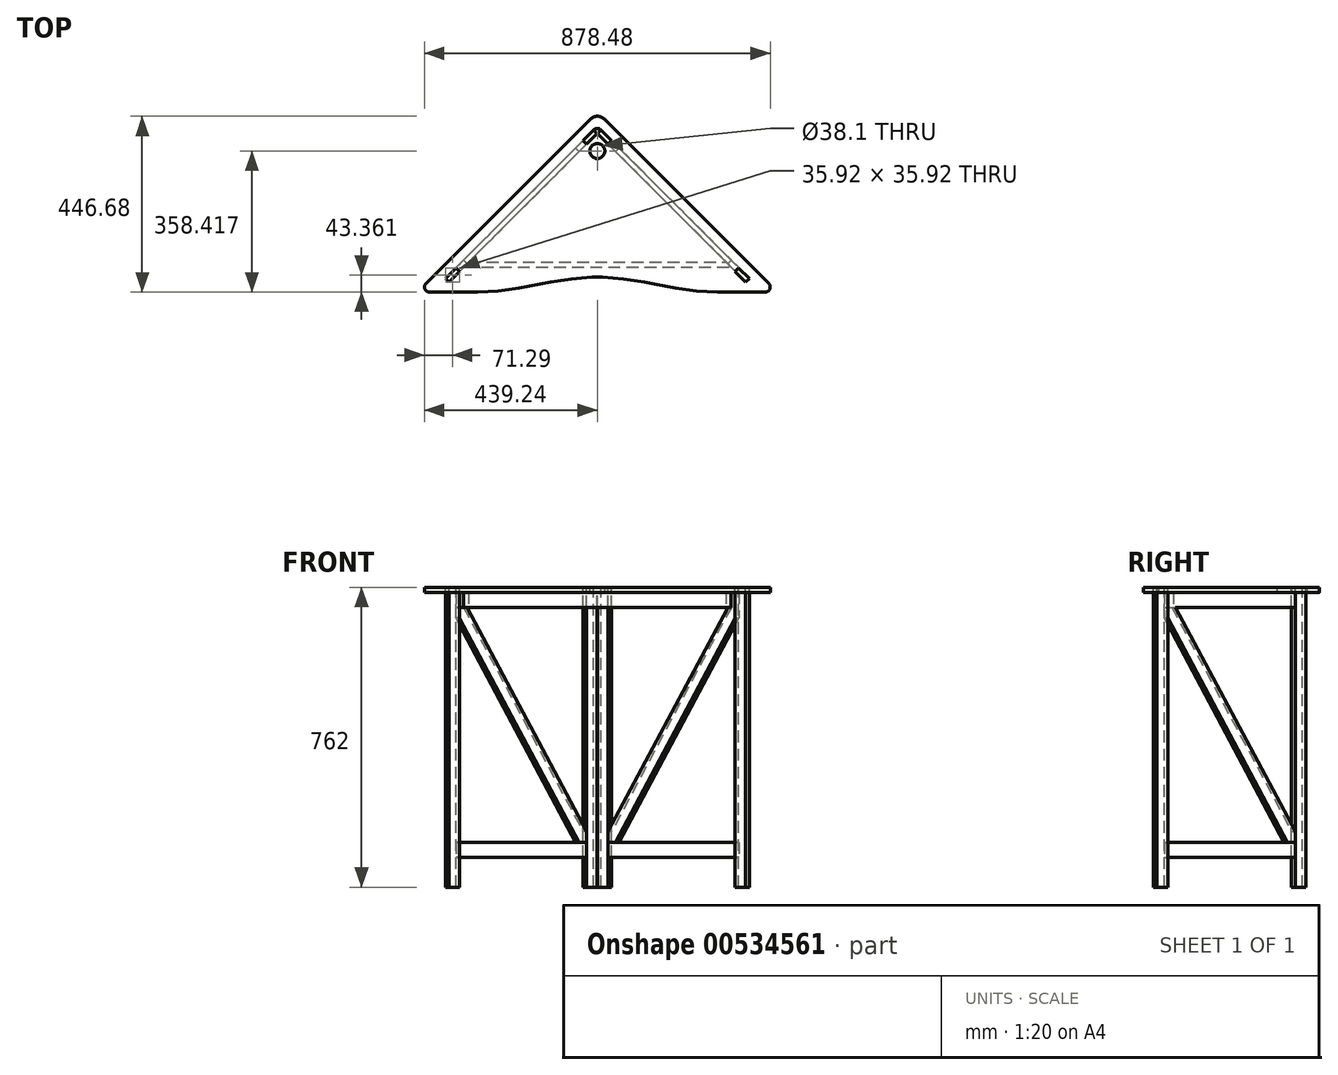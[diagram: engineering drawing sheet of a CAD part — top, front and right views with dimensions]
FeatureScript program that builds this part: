
annotation { "Feature Type Name" : "Feature", "Feature Type Description" : "" }
export const myFeature = defineFeature(function(context is Context, id is Id, definition is map)
    precondition{}
    {
        {
            var Q0;
            Q0=qCreatedBy(makeId("Top.planeOp"),FACE);
            var sketch = newSketch(context, id + "F0", { "sketchPlane" : qUnion([Q0])});
            skLineSegment(sketch, "E0", {"start": v(0, 457.2) * mm, "end": v(228.6, 228.6) * mm, "construction": true});
            skLineSegment(sketch, "E1", {"start": v(457.2, 0) * mm, "end": v(0, 0) * mm, "construction": true});
            skLineSegment(sketch, "E2", {"start": v(-228.6, 228.6) * mm, "end": v(0, 0) * mm, "construction": true});
            skLineSegment(sketch, "E3", {"start": v(0, 0) * mm, "end": v(228.6, 228.6) * mm, "construction": true});
            skLineSegment(sketch, "E4", {"start": v(0, 0) * mm, "end": v(0, 457.2) * mm, "construction": true});
            skLineSegment(sketch, "E5", {"start": v(-228.6, 228.6) * mm, "end": v(0, 457.2) * mm, "construction": true});
            skLineSegment(sketch, "E6", {"start": v(228.6, 228.6) * mm, "end": v(457.2, 0) * mm, "construction": true});
            skLineSegment(sketch, "E7", {"start": v(0, 0) * mm, "end": v(-457.2, 0) * mm, "construction": true});
            skPoint(sketch, "E8.visualSharp", {"position": v(-457.2, 0) * mm});
            skPoint(sketch, "E9.visualSharp", {"position": v(457.2, 0) * mm});
            skPoint(sketch, "E10.visualSharp", {"position": v(0, 457.2) * mm});
            skLineSegment(sketch, "E11", {"start": v(-228.6, 228.6) * mm, "end": v(-457.2, 0) * mm, "construction": true});
            skSolve(sketch);
        }
        {
            var Q0;
            Q0=qCreatedBy(makeId("Top.planeOp"),FACE);
            var sketch = newSketch(context, id + "F1", { "sketchPlane" : qUnion([Q0])});
            skLineSegment(sketch, "E12", {"start": v(17.96, 439.24) * mm, "end": v(435.52, 21.68) * mm});
            skLineSegment(sketch, "E13", {"start": v(-435.52, 21.68) * mm, "end": v(-17.96, 439.24) * mm});
            skLineSegment(sketch, "E14", {"start": v(-426.54, 0) * mm, "end": v(-304.8, 0) * mm});
            skLineSegment(sketch, "E15", {"start": v(304.8, 0) * mm, "end": v(426.54, 0) * mm});
            skLineSegment(sketch, "E16", {"start": v(-304.8, 0) * mm, "end": v(-203.2, 0) * mm, "construction": true});
            skLineSegment(sketch, "E17", {"start": v(304.8, 0) * mm, "end": v(203.2, 0) * mm, "construction": true});
            skFitSpline(sketch, "E18", {"points": [v(-304.8, 0) * mm, v(0, 38.1) * mm, v(304.8, 0) * mm], "startDerivative": vector(609.6, 0) * mm, "endDerivative": vector(609.6, 0) * mm});
            skPoint(sketch, "E19.visualSharp", {"position": v(-457.2, 0) * mm});
            skArc(sketch, "E19.filletArc", {"start": v(-435.52, 21.68) * mm, "mid": v(-438.27, 7.84) * mm, "end": v(-426.54, 0) * mm});
            skPoint(sketch, "E20.visualSharp", {"position": v(457.2, 0) * mm});
            skArc(sketch, "E20.filletArc", {"start": v(426.54, 0) * mm, "mid": v(438.27, 7.84) * mm, "end": v(435.52, 21.68) * mm});
            skPoint(sketch, "E21.visualSharp", {"position": v(0, 457.2) * mm});
            skArc(sketch, "E21.filletArc", {"start": v(17.96, 439.24) * mm, "mid": v(0, 446.68) * mm, "end": v(-17.96, 439.24) * mm});
            skSolve(sketch);
        }
        {
            var Q0;
            Q0=qCreatedBy(makeId("Top.planeOp"),FACE);
            var sketch = newSketch(context, id + "F2", { "sketchPlane" : qUnion([Q0])});
            skLineSegment(sketch, "E22", {"start": v(-0.25, 403.06) * mm, "end": v(-27.2, 376.12) * mm});
            skLineSegment(sketch, "E23", {"start": v(-27.2, 376.12) * mm, "end": v(-36.18, 385.1) * mm});
            skLineSegment(sketch, "E24", {"start": v(-36.18, 385.1) * mm, "end": v(-9.23, 412.04) * mm});
            skLineSegment(sketch, "E25", {"start": v(-9.23, 412.04) * mm, "end": v(-0.25, 403.06) * mm});
            skLineSegment(sketch, "E26.MirrorCS", {"start": v(-385.91, 34.38) * mm, "end": v(-376.93, 25.4) * mm});
            skLineSegment(sketch, "E27.MirrorCS", {"start": v(-349.99, 52.34) * mm, "end": v(-358.97, 61.32) * mm});
            skLineSegment(sketch, "E28.MirrorCS", {"start": v(-358.97, 61.32) * mm, "end": v(-385.91, 34.38) * mm});
            skLineSegment(sketch, "E29.MirrorCS", {"start": v(-376.93, 25.4) * mm, "end": v(-349.99, 52.34) * mm});
            skLineSegment(sketch, "E30.MirrorCS", {"start": v(349.99, 52.34) * mm, "end": v(358.97, 61.32) * mm});
            skLineSegment(sketch, "E31.MirrorCS", {"start": v(385.91, 34.38) * mm, "end": v(376.93, 25.4) * mm});
            skLineSegment(sketch, "E32.MirrorCS", {"start": v(376.93, 25.4) * mm, "end": v(349.99, 52.34) * mm});
            skLineSegment(sketch, "E33.MirrorCS", {"start": v(358.97, 61.32) * mm, "end": v(385.91, 34.38) * mm});
            skLineSegment(sketch, "E34.MirrorCS", {"start": v(9.23, 412.04) * mm, "end": v(0.25, 403.06) * mm});
            skLineSegment(sketch, "E35.MirrorCS", {"start": v(27.2, 376.12) * mm, "end": v(36.18, 385.1) * mm});
            skLineSegment(sketch, "E36.MirrorCS", {"start": v(36.18, 385.1) * mm, "end": v(9.23, 412.04) * mm});
            skLineSegment(sketch, "E37.MirrorCS", {"start": v(0.25, 403.06) * mm, "end": v(27.2, 376.12) * mm});
            skCircle(sketch, "E38", {"center": v(0, 358.42) * mm, "radius": 19.05 * mm});
            skArc(sketch, "E39", {"start": v(9.23, 412.04) * mm, "mid": v(0, 415.87) * mm, "end": v(-9.23, 412.04) * mm});
            skArc(sketch, "E40", {"start": v(0.25, 403.06) * mm, "mid": v(0, 403.17) * mm, "end": v(-0.25, 403.06) * mm});
            skSolve(sketch);
        }
        {
            var Q0;
            Q0=makeQuery(id+"F1.imprint","IMPRINT",FACE,{"disambiguationData":[TD([[makeQuery(id+"F1.imprint","IMPRINT",EDGE,{"derivedFrom":sQuery(id+"F1.wireOp",EDGE,"E12")}),-1.0]])]});
            extrude(context, id + "F3", {"entities" : qUnion([Q0]), "oppositeDirection" : true, "depth" : 12.7 * mm, "offsetDistance" : 25.4 * mm});
        }
        {
            var Q0;
            Q0 = qSketchRegion(id + "F2", true);
            extrude(context, id + "F4", {"entities" : qUnion([Q0]), "operationType" : NewBodyOperationType.REMOVE, "endBound" : BoundingType.UP_TO_NEXT, "oppositeDirection" : true, "depth" : 25.4 * mm, "offsetDistance" : 25.4 * mm});
        }
        {
            var Q0;
            Q0=makeQuery(id+"F2.imprint","IMPRINT",FACE,{"disambiguationData":[TD([[makeQuery(id+"F2.imprint","IMPRINT",EDGE,{"derivedFrom":sQuery(id+"F2.wireOp",EDGE,"E26.MirrorCS")}),1.0]])]});
            var Q1;
            Q1=makeQuery(id+"F2.imprint","IMPRINT",FACE,{"disambiguationData":[TD([[makeQuery(id+"F2.imprint","IMPRINT",EDGE,{"derivedFrom":sQuery(id+"F2.wireOp",EDGE,"E30.MirrorCS")}),-1.0]])]});
            var Q2;
            Q2=makeQuery(id+"F2.imprint","IMPRINT",FACE,{"disambiguationData":[TD([[makeQuery(id+"F2.imprint","IMPRINT",EDGE,{"derivedFrom":sQuery(id+"F2.wireOp",EDGE,"E34.MirrorCS")}),1.0]])]});
            var Q3;
            Q3=makeQuery(id+"F2.imprint","IMPRINT",FACE,{"disambiguationData":[TD([[makeQuery(id+"F2.imprint","IMPRINT",EDGE,{"derivedFrom":sQuery(id+"F2.wireOp",EDGE,"E22")}),-1.0]])]});
            var Q4;
            Q4=sQuery(id+"F2.wireOp",EDGE,"E22");
            var Q5;
            Q5=sQuery(id+"F2.wireOp",EDGE,"E23");
            var Q6;
            Q6=sQuery(id+"F2.wireOp",EDGE,"E24");
            var Q7;
            Q7=sQuery(id+"F2.wireOp",EDGE,"E25");
            var Q8;
            Q8=sQuery(id+"F2.wireOp",EDGE,"E26.MirrorCS");
            var Q9;
            Q9=sQuery(id+"F2.wireOp",EDGE,"E27.MirrorCS");
            var Q10;
            Q10=sQuery(id+"F2.wireOp",EDGE,"E28.MirrorCS");
            var Q11;
            Q11=sQuery(id+"F2.wireOp",EDGE,"E29.MirrorCS");
            var Q12;
            Q12=sQuery(id+"F2.wireOp",EDGE,"E30.MirrorCS");
            var Q13;
            Q13=sQuery(id+"F2.wireOp",EDGE,"E31.MirrorCS");
            var Q14;
            Q14=sQuery(id+"F2.wireOp",EDGE,"E32.MirrorCS");
            var Q15;
            Q15=sQuery(id+"F2.wireOp",EDGE,"E33.MirrorCS");
            var Q16;
            Q16=sQuery(id+"F2.wireOp",EDGE,"E34.MirrorCS");
            var Q17;
            Q17=sQuery(id+"F2.wireOp",EDGE,"E35.MirrorCS");
            var Q18;
            Q18=sQuery(id+"F2.wireOp",EDGE,"E36.MirrorCS");
            var Q19;
            Q19=sQuery(id+"F2.wireOp",EDGE,"E37.MirrorCS");
            var Q20;
            Q20=sQuery(id+"F2.wireOp",EDGE,"E40");
            extrude(context, id + "F5", {"entities" : qUnion([Q0, Q1, Q2, Q3]), "surfaceEntities" : qUnion([Q4, Q5, Q6, Q7, Q8, Q9, Q10, Q11, Q12, Q13, Q14, Q15, Q16, Q17, Q18, Q19, Q20]), "oppositeDirection" : true, "depth" : 762 * mm, "offsetDistance" : 25.4 * mm});
        }
        {
            var Q0;
            Q0=makeQuery(id+"F5.opExtrude","SWEPT_FACE",FACE,{"disambiguationData":[OSD([sQuery(id+"F2.wireOp",EDGE,"E23")])]});
            var sketch = newSketch(context, id + "F6", { "sketchPlane" : qUnion([Q0])});
            skLineSegment(sketch, "E41.bottom", {"start": v(-297.89, -12.7) * mm, "end": v(-285.19, -12.7) * mm});
            skLineSegment(sketch, "E41.top", {"start": v(-297.89, -50.8) * mm, "end": v(-285.19, -50.8) * mm});
            skLineSegment(sketch, "E41.left", {"start": v(-297.89, -12.7) * mm, "end": v(-297.89, -50.8) * mm});
            skLineSegment(sketch, "E41.right", {"start": v(-285.19, -12.7) * mm, "end": v(-285.19, -50.8) * mm});
            skLineSegment(sketch, "E42.bottom", {"start": v(-297.89, -647.7) * mm, "end": v(-285.19, -647.7) * mm});
            skLineSegment(sketch, "E42.top", {"start": v(-297.89, -685.8) * mm, "end": v(-285.19, -685.8) * mm});
            skLineSegment(sketch, "E42.left", {"start": v(-297.89, -647.7) * mm, "end": v(-297.89, -685.8) * mm});
            skLineSegment(sketch, "E42.right", {"start": v(-285.19, -647.7) * mm, "end": v(-285.19, -685.8) * mm});
            skSolve(sketch);
        }
        {
            var Q0;
            Q0 = qSketchRegion(id + "F6", true);
            var Q1;
            Q1=makeQuery(id+"F5.opExtrude","SWEPT_FACE",FACE,{"disambiguationData":[OSD([sQuery(id+"F2.wireOp",EDGE,"E27.MirrorCS")])]});
            var Q2;
            Q2=makeQuery(id+"F5.opExtrude","SWEPT_BODY",BODY,{"disambiguationData":[OSD([sQuery(id+"F2.wireOp",EDGE,"E26.MirrorCS"),sQuery(id+"F2.wireOp",EDGE,"E27.MirrorCS"),sQuery(id+"F2.wireOp",EDGE,"E28.MirrorCS"),sQuery(id+"F2.wireOp",EDGE,"E29.MirrorCS")])]});
            extrude(context, id + "F7", {"entities" : qUnion([Q0]), "endBound" : BoundingType.UP_TO_SURFACE, "depth" : 762 * mm, "endBoundEntityFace" : qUnion([Q1]), "endBoundEntityBody" : qUnion([Q2]), "offsetDistance" : 25.4 * mm});
        }
        {
            var Q0;
            Q0=makeQuery(id+"F5.opExtrude","SWEPT_FACE",FACE,{"disambiguationData":[OSD([sQuery(id+"F2.wireOp",EDGE,"E24")])]});
            var sketch = newSketch(context, id + "F8", { "sketchPlane" : qUnion([Q0])});
            skLineSegment(sketch, "E43", {"start": v(210.47, -50.8) * mm, "end": v(183.27, -50.8) * mm});
            skLineSegment(sketch, "E44", {"start": v(183.27, -50.8) * mm, "end": v(-246.73, -620.5) * mm});
            skLineSegment(sketch, "E45", {"start": v(-246.73, -620.5) * mm, "end": v(-246.73, -647.7) * mm});
            skLineSegment(sketch, "E46", {"start": v(-246.73, -647.7) * mm, "end": v(-219.53, -647.7) * mm});
            skLineSegment(sketch, "E47", {"start": v(-219.53, -647.7) * mm, "end": v(210.47, -78) * mm});
            skLineSegment(sketch, "E48", {"start": v(210.47, -78) * mm, "end": v(210.47, -50.8) * mm});
            skSolve(sketch);
        }
        {
            var Q0;
            Q0=makeQuery(id+"F8.imprint","IMPRINT",FACE,{"disambiguationData":[TD([[makeQuery(id+"F8.imprint","IMPRINT",EDGE,{"derivedFrom":sQuery(id+"F8.wireOp",EDGE,"E43")}),1.0]])]});
            extrude(context, id + "F9", {"entities" : qUnion([Q0]), "oppositeDirection" : true, "depth" : 12.7 * mm, "offsetDistance" : 25.4 * mm});
        }
        {
            var Q0;
            Q0=makeQuery(id+"F7.opExtrude","SWEPT_BODY",BODY,{"disambiguationData":[OSD([sQuery(id+"F6.wireOp",EDGE,"E42.bottom"),sQuery(id+"F6.wireOp",EDGE,"E42.top"),sQuery(id+"F6.wireOp",EDGE,"E42.left"),sQuery(id+"F6.wireOp",EDGE,"E42.right")])]});
            var Q1;
            Q1=makeQuery(id+"F7.opExtrude","SWEPT_BODY",BODY,{"disambiguationData":[OSD([sQuery(id+"F6.wireOp",EDGE,"E41.bottom"),sQuery(id+"F6.wireOp",EDGE,"E41.top"),sQuery(id+"F6.wireOp",EDGE,"E41.left"),sQuery(id+"F6.wireOp",EDGE,"E41.right")])]});
            var Q2;
            Q2=makeQuery(id+"F9.opExtrude","SWEPT_BODY",BODY,{"disambiguationData":[OSD([sQuery(id+"F8.wireOp",EDGE,"E43"),sQuery(id+"F8.wireOp",EDGE,"E44"),sQuery(id+"F8.wireOp",EDGE,"E45"),sQuery(id+"F8.wireOp",EDGE,"E46"),sQuery(id+"F8.wireOp",EDGE,"E47"),sQuery(id+"F8.wireOp",EDGE,"E48")])]});
            var Q3;
            Q3=qCreatedBy(makeId("Right.planeOp"),FACE);
            mirror(context, id + "F10", {"entities" : qUnion([Q0, Q1, Q2]), "mirrorPlane" : qUnion([Q3])});
        }
        {
            var Q0;
            Q0=qCreatedBy(makeId("Right.planeOp"),FACE);
            var sketch = newSketch(context, id + "F11", { "sketchPlane" : qUnion([Q0])});
            skLineSegment(sketch, "E49.bottom", {"start": v(63.5, -12.7) * mm, "end": v(76.2, -12.7) * mm});
            skLineSegment(sketch, "E49.top", {"start": v(63.5, -50.8) * mm, "end": v(76.2, -50.8) * mm});
            skLineSegment(sketch, "E49.left", {"start": v(63.5, -12.7) * mm, "end": v(63.5, -50.8) * mm});
            skLineSegment(sketch, "E49.right", {"start": v(76.2, -12.7) * mm, "end": v(76.2, -50.8) * mm});
            skSolve(sketch);
        }
        {
            var Q0;
            Q0 = qSketchRegion(id + "F11", true);
            var Q1;
            Q1=makeQuery(id+"F7.opExtrude","SWEPT_FACE",FACE,{"disambiguationData":[OSD([sQuery(id+"F6.wireOp",EDGE,"E41.right")])]});
            extrude(context, id + "F12", {"entities" : qUnion([Q0]), "endBound" : BoundingType.UP_TO_SURFACE, "oppositeDirection" : true, "depth" : 25.4 * mm, "endBoundEntityFace" : qUnion([Q1]), "offsetDistance" : 25.4 * mm});
        }
        {
            var Q0;
            Q0=makeQuery(id+"F11.imprint","IMPRINT",FACE,{"disambiguationData":[TD([[makeQuery(id+"F11.imprint","IMPRINT",EDGE,{"derivedFrom":sQuery(id+"F11.wireOp",EDGE,"E49.bottom")}),-1.0]])]});
            var Q1;
            Q1=makeQuery(id+"F10.opPattern","COPY",FACE,{"derivedFrom":makeQuery(id+"F7.opExtrude","SWEPT_FACE",FACE,{"disambiguationData":[OSD([sQuery(id+"F6.wireOp",EDGE,"E41.right")])]}),"instanceName":"1"});
            extrude(context, id + "F13", {"entities" : qUnion([Q0]), "operationType" : NewBodyOperationType.ADD, "endBound" : BoundingType.UP_TO_SURFACE, "depth" : 25.4 * mm, "endBoundEntityFace" : qUnion([Q1]), "offsetDistance" : 25.4 * mm});
        }
    });
